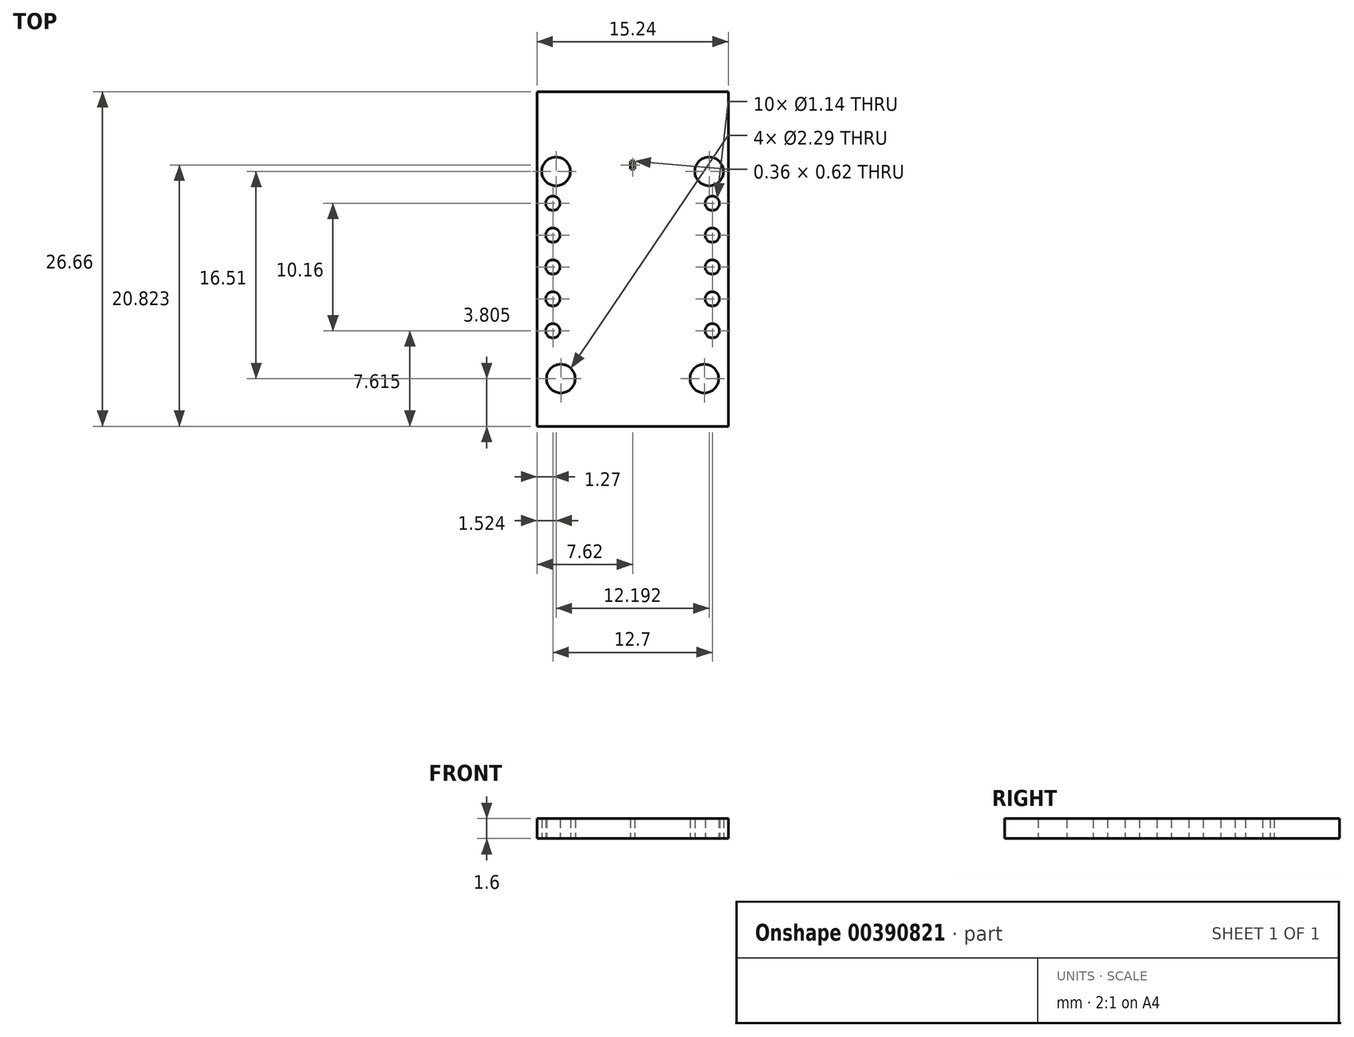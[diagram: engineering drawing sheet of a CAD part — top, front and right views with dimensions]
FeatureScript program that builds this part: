
annotation { "Feature Type Name" : "Feature", "Feature Type Description" : "" }
export const myFeature = defineFeature(function(context is Context, id is Id, definition is map)
    precondition{}
    {
        {
            var Q0;
            Q0=qCreatedBy(makeId("Top.planeOp"),FACE);
            var sketch = newSketch(context, id + "F0", { "sketchPlane" : qUnion([Q0])});
            skLineSegment(sketch, "E0.bottom", {"start": v(-7.62, 13.34) * mm, "end": v(7.62, 13.34) * mm});
            skLineSegment(sketch, "E0.top", {"start": v(-7.62, -13.34) * mm, "end": v(7.62, -13.34) * mm});
            skLineSegment(sketch, "E0.left", {"start": v(-7.62, 13.34) * mm, "end": v(-7.62, -13.33) * mm});
            skLineSegment(sketch, "E0.right", {"start": v(7.62, 13.34) * mm, "end": v(7.62, -13.33) * mm});
            skPoint(sketch, "E0.middle", {"position": v(0, 0) * mm});
            skCircle(sketch, "E1", {"center": v(5.72, -9.52) * mm, "radius": 1.14 * mm});
            skCircle(sketch, "E2", {"center": v(6.35, -5.71) * mm, "radius": 0.57 * mm});
            skCircle(sketch, "E3", {"center": v(6.1, 6.99) * mm, "radius": 1.14 * mm});
            skCircle(sketch, "E4.1.0.0", {"center": v(6.35, -3.17) * mm, "radius": 0.57 * mm});
            skCircle(sketch, "E4.2.0.0", {"center": v(6.35, -0.63) * mm, "radius": 0.57 * mm});
            skCircle(sketch, "E4.3.0.0", {"center": v(6.35, 1.9) * mm, "radius": 0.57 * mm});
            skCircle(sketch, "E4.4.0.0", {"center": v(6.35, 4.45) * mm, "radius": 0.57 * mm});
            skLineSegment(sketch, "E4.direction1", {"start": v(6.35, -5.71) * mm, "end": v(6.35, -3.17) * mm, "construction": true});
            skLineSegment(sketch, "E5", {"start": v(0, 22.9) * mm, "end": v(0, -49.1) * mm, "construction": true});
            skCircle(sketch, "E6.MirrorC", {"center": v(-5.72, -9.52) * mm, "radius": 1.14 * mm});
            skCircle(sketch, "E7.MirrorC", {"center": v(-6.35, -5.71) * mm, "radius": 0.57 * mm});
            skCircle(sketch, "E8.MirrorC", {"center": v(-6.35, -3.17) * mm, "radius": 0.57 * mm});
            skCircle(sketch, "E9.MirrorC", {"center": v(-6.35, -0.63) * mm, "radius": 0.57 * mm});
            skCircle(sketch, "E10.MirrorC", {"center": v(-6.35, 4.45) * mm, "radius": 0.57 * mm});
            skCircle(sketch, "E11.MirrorC", {"center": v(-6.35, 1.9) * mm, "radius": 0.57 * mm});
            skCircle(sketch, "E12.MirrorC", {"center": v(-6.1, 6.99) * mm, "radius": 1.14 * mm});
            skLineSegment(sketch, "E13.bottom", {"start": v(-0.18, 7.8) * mm, "end": v(0.18, 7.8) * mm});
            skLineSegment(sketch, "E13.top", {"start": v(-0.18, 7.18) * mm, "end": v(0.18, 7.18) * mm});
            skLineSegment(sketch, "E13.left", {"start": v(-0.18, 7.8) * mm, "end": v(-0.18, 7.18) * mm});
            skLineSegment(sketch, "E13.right", {"start": v(0.18, 7.8) * mm, "end": v(0.18, 7.18) * mm});
            skPoint(sketch, "E13.middle", {"position": v(0, 7.5) * mm});
            skSolve(sketch);
        }
        {
            var Q0;
            Q0 = qSketchRegion(id + "F0", true);
            extrude(context, id + "F1", {"entities" : qUnion([Q0]), "depth" : 1.6 * mm});
        }
    });
